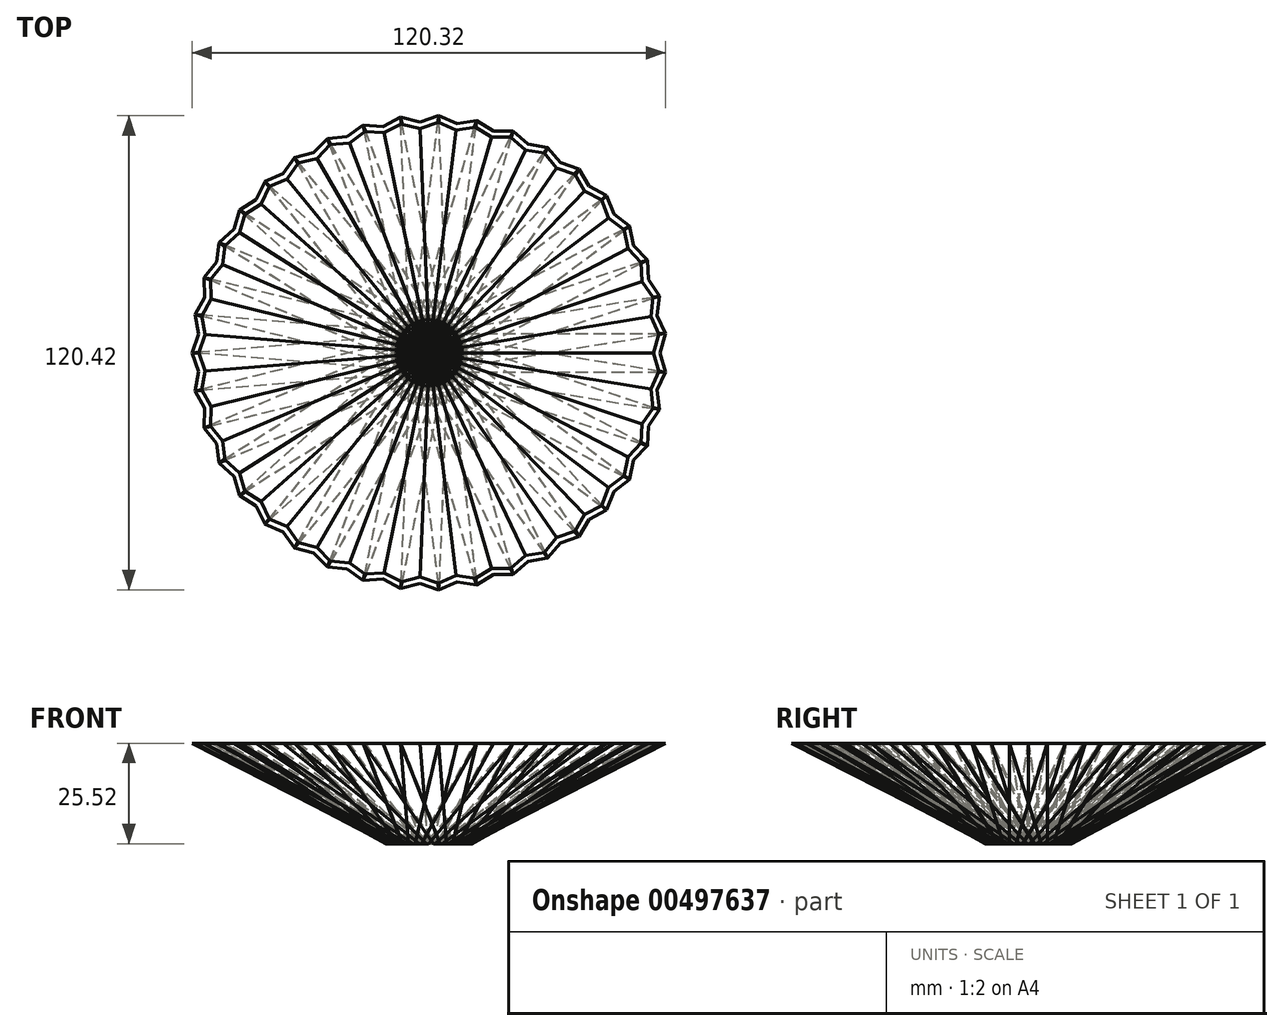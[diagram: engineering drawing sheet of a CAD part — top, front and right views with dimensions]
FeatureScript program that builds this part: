
annotation { "Feature Type Name" : "Feature", "Feature Type Description" : "" }
export const myFeature = defineFeature(function(context is Context, id is Id, definition is map)
    precondition{}
    {
        {
            var Q0;
            Q0=qCreatedBy(makeId("Front.planeOp"),FACE);
            var sketch = newSketch(context, id + "F0", { "sketchPlane" : qUnion([Q0])});
            skLineSegment(sketch, "E0", {"start": v(0, 0) * mm, "end": v(8.4, 0) * mm});
            skLineSegment(sketch, "E1", {"start": v(8.8, 1.04) * mm, "end": v(17.73, 24.89) * mm});
            skLineSegment(sketch, "E2", {"start": v(17.73, 24.89) * mm, "end": v(14.25, 52.02) * mm});
            skLineSegment(sketch, "E3.0", {"start": v(15.58, 25.14) * mm, "end": v(12.13, 52.02) * mm});
            skLineSegment(sketch, "E3.1", {"start": v(6.95, 2.1) * mm, "end": v(15.58, 25.14) * mm});
            skLineSegment(sketch, "E3.2", {"start": v(0, 2.1) * mm, "end": v(6.95, 2.1) * mm});
            skLineSegment(sketch, "E4", {"start": v(14.25, 52.02) * mm, "end": v(12.13, 52.02) * mm});
            skLineSegment(sketch, "E5", {"start": v(0, 2.1) * mm, "end": v(0, 0) * mm});
            skLineSegment(sketch, "E6", {"start": v(17.73, 24.89) * mm, "end": v(15.49, 24.89) * mm});
            skLineSegment(sketch, "E7.0", {"start": v(7.89, 0.75) * mm, "end": v(17.03, 25.15) * mm});
            skLineSegment(sketch, "E7.1", {"start": v(0, 0.75) * mm, "end": v(8.23, 0.75) * mm});
            skLineSegment(sketch, "E8", {"start": v(8.4, 0) * mm, "end": v(58.7, 25.52) * mm});
            skLineSegment(sketch, "E9.0", {"start": v(8.23, 0.75) * mm, "end": v(57.04, 25.52) * mm});
            skLineSegment(sketch, "E10", {"start": v(58.7, 25.52) * mm, "end": v(57.04, 25.52) * mm});
            skSolve(sketch);
        }
        {
            var Q0;
            Q0=qCreatedBy(makeId("Top.planeOp"),FACE);
            var sketch = newSketch(context, id + "F1", { "sketchPlane" : qUnion([Q0])});
            skLineSegment(sketch, "E11", {"start": v(0, 0) * mm, "end": v(0.83, 1.39) * mm});
            skLineSegment(sketch, "E12", {"start": v(0.83, 1.39) * mm, "end": v(1.36, 4.85) * mm});
            skPoint(sketch, "E13.orphan", {"position": v(1.65, 2.78) * mm});
            skPoint(sketch, "E14.orphan", {"position": v(1.65, 6.74) * mm});
            skLineSegment(sketch, "E15", {"start": v(0, 0) * mm, "end": v(1.36, 4.85) * mm});
            skSolve(sketch);
        }
        {
            var Q0;
            {var subQ1=sQuery(id+"F0.wireOp",EDGE,"E0");Q0=makeQuery(id+"F0.imprint","IMPRINT",FACE,{"disambiguationData":[TD([[makeQuery(id+"F0.imprint","IMPRINT",EDGE,{"derivedFrom":subQ1}),1.0]])]});}
            var Q1;
            Q1=sQuery(id+"F1.wireOp",EDGE,"EZPR2Nsh-NOnx-jhEP-Uec3-nZ7E1FM0hnEN");
            var Q2;
            Q2=sQuery(id+"F1.wireOp",EDGE,"E15");
            sweep(context, id + "F2", {"profiles" : qUnion([Q0]), "path" : qUnion([Q1, Q2])});
        }
        {
            var Q0;
            Q0=makeQuery(id+"F2.opSweep","SWEPT_BODY",BODY,{"disambiguationData":[OSD([sQuery(id+"F0.wireOp",EDGE,"E0"),sQuery(id+"F0.wireOp",EDGE,"E1"),sQuery(id+"F0.wireOp",EDGE,"E5"),sQuery(id+"F0.wireOp",EDGE,"E6"),sQuery(id+"F0.wireOp",EDGE,"E7.0"),sQuery(id+"F0.wireOp",EDGE,"E7.1"),sQuery(id+"F1.wireOp",EDGE,"E11")])]});
            var Q1;
            {var subQ1=sQuery(id+"F0.wireOp",EDGE,"E3.2");Q1=makeQuery(id+"F0.imprint","IMPRINT",FACE,{"disambiguationData":[TD([[makeQuery(id+"F0.imprint","IMPRINT",EDGE,{"derivedFrom":subQ1}),-1.0]])]});}
            mirror(context, id + "F3", {"operationType" : NewBodyOperationType.ADD, "entities" : qUnion([Q0]), "mirrorPlane" : qUnion([Q1])});
        }
        {
            var Q0;
            Q0=makeQuery(id+"F2.opSweep","SWEPT_BODY",BODY,{"disambiguationData":[OSD([sQuery(id+"F0.wireOp",EDGE,"E0"),sQuery(id+"F0.wireOp",EDGE,"E1"),sQuery(id+"F0.wireOp",EDGE,"E5"),sQuery(id+"F0.wireOp",EDGE,"E6"),sQuery(id+"F0.wireOp",EDGE,"E7.0"),sQuery(id+"F0.wireOp",EDGE,"E7.1"),sQuery(id+"F1.wireOp",EDGE,"E11")])]});
            var Q1;
            Q1=sQuery(id+"F0.wireOp",EDGE,"E5");
            circularPattern(context, id + "F4", {"entities" : qUnion([Q0]), "axis" : qUnion([Q1]), "angle" : 360 * degree, "instanceCount" : 39, "equalSpace" : true});
        }
    });
